FCSTD DOCUMENT  (FreeCAD 1.0R39109 (Git))
Label: MotorFinAssembly
License: Creative Commons Attribution-ShareAlike 4.0
LicenseURL: https://creativecommons.org/licenses/by-sa/4.0/
objects: App::FeaturePython×19, App::Link×18, Assembly::ViewGroup×1, Assembly::JointGroup×1, Assembly::AssemblyObject×1
EXTERNAL_REF file=CenteringRing.FCStd obj=Body
EXTERNAL_REF file=Fin.FCStd obj=Body
EXTERNAL_REF file=DowelNut.FCStd obj=Part__Feature
EXTERNAL_REF file=MMT.FCStd obj=Body
EXTERNAL_REF file=ThrustPlate-4in-AeroPack.FCStd obj=Body
EXTERNAL_REF file=Retainer-54mm-AeroPack.FCStd obj=Body

FEATURE [App::Link] Body  label="Mid Centering Ring"
  LinkedObject = -> <external CenteringRing.FCStd>#Body
FEATURE [App::FeaturePython] GroundedJoint  # Assembly grounded joint (typed FeaturePython)
  ObjectToGround = -> Body
FEATURE [App::Link] Body001  label="Fin001"
  LinkPlacement = pos=(-32.6984,-36.7997,37) rot=(0.678598,-0.281085,-0.678598;3.68962rad)
  LinkedObject = -> <external Fin.FCStd>#Body
  Placement = pos=(-32.6984,-36.7997,37) rot=(0.678598,-0.281085,-0.678598;3.68962rad)
FEATURE [App::FeaturePython] Joint  label="Fixed"  # Assembly joint (typed FeaturePython)
  Activated = true
  AngleMax = 0
  AngleMin = 0
  Detach1 = false
  Detach2 = false
  Distance = 0
  Distance2 = 0
  EnableAngleMax = false
  EnableAngleMin = false
  EnableLengthMax = false
  EnableLengthMin = false
  JointType = 0 (Fixed)
  LengthMax = 0
  LengthMin = 0
  Offset2 = pos=(0,0,0) rot=(0,0,-1;1.5708rad)
  Placement1 = pos=(-27.6426,-27.6426,5.8) rot=(0.281085,0.678598,0.678598;2.59356rad)
  Placement2 = pos=(31.2,-10.05,2.9) rot=(-0.57735,0.57735,-0.57735;4.18879rad)
  Reference1 = -> Assembly [Body.Face14,Body.Face14]
  Reference2 = -> Assembly [Body001.Face10,Body001.Face10]
FEATURE [App::Link] _0835A220_Dowel_Nuts_for_Wood  label="90835A220_Dowel Nuts for Wood"
  LinkPlacement = pos=(1.4e-15,-39.2,6.12086) rot=(0.707107,0,0.707107;3.14159rad)
  LinkedObject = -> <external DowelNut.FCStd>#Part__Feature
  Placement = pos=(1.4e-15,-39.2,6.12086) rot=(0.707107,0,0.707107;3.14159rad)
FEATURE [App::FeaturePython] Joint001  label="Fixed001"  # Assembly joint (typed FeaturePython)
  Activated = true
  AngleMax = 0
  AngleMin = 0
  Detach1 = false
  Detach2 = false
  Distance = 0
  Distance2 = 0
  EnableAngleMax = false
  EnableAngleMin = false
  EnableLengthMax = false
  EnableLengthMin = false
  JointType = 0 (Fixed)
  LengthMax = 0
  LengthMin = 0
  Placement1 = pos=(0,-39.2,0) rot=(0,0,1;0rad)
  Placement2 = pos=(-6.12086,0,0) rot=(0,-1,0;1.5708rad)
  Reference1 = -> Assembly [Body.Edge29,Body.Edge29]
  Reference2 = -> Assembly [_0835A220_Dowel_Nuts_for_Wood.Edge144,_0835A220_Dowel_Nuts_for_Wood.Edge144]
FEATURE [App::Link] Body002  label="Fin002"
  LinkPlacement = pos=(36.7997,-32.6984,37) rot=(0.678598,0.281085,-0.678598;2.59356rad)
  LinkedObject = -> <external Fin.FCStd>#Body
  Placement = pos=(36.7997,-32.6984,37) rot=(0.678598,0.281085,-0.678598;2.59356rad)
FEATURE [App::Link] Body003  label="Fin003"
  LinkPlacement = pos=(32.6984,36.7997,37) rot=(0.357407,0.862856,-0.357407;1.71777rad)
  LinkedObject = -> <external Fin.FCStd>#Body
  Placement = pos=(32.6984,36.7997,37) rot=(0.357407,0.862856,-0.357407;1.71777rad)
FEATURE [App::Link] Body004  label="Fin004"
  LinkPlacement = pos=(-36.7997,32.6984,37) rot=(-0.357407,0.862856,0.357407;1.71777rad)
  LinkedObject = -> <external Fin.FCStd>#Body
  Placement = pos=(-36.7997,32.6984,37) rot=(-0.357407,0.862856,0.357407;1.71777rad)
FEATURE [App::FeaturePython] Joint002  label="Fixed002"  # Assembly joint (typed FeaturePython)
  Activated = true
  AngleMax = 0
  AngleMin = 0
  Detach1 = false
  Detach2 = false
  Distance = 0
  Distance2 = 0
  EnableAngleMax = false
  EnableAngleMin = false
  EnableLengthMax = false
  EnableLengthMin = false
  JointType = 0 (Fixed)
  LengthMax = 0
  LengthMin = 0
  Offset2 = pos=(0,0,0) rot=(0,0,1;1.5708rad)
  Placement1 = pos=(31.2,-10.05,2.9) rot=(0,-0.707107,0.707107;3.14159rad)
  Placement2 = pos=(27.6426,-27.6426,5.8) rot=(0.357407,0.862856,0.357407;4.56541rad)
  Reference1 = -> Assembly [Body002.Face10,Body002.Face10]
  Reference2 = -> Assembly [Body.Face8,Body.Face8]
FEATURE [App::FeaturePython] Joint003  label="Fixed003"  # Assembly joint (typed FeaturePython)
  Activated = true
  AngleMax = 0
  AngleMin = 0
  Detach1 = false
  Detach2 = false
  Distance = 0
  Distance2 = 0
  EnableAngleMax = false
  EnableAngleMin = false
  EnableLengthMax = false
  EnableLengthMin = false
  JointType = 0 (Fixed)
  LengthMax = 0
  LengthMin = 0
  Offset2 = pos=(0,0,0) rot=(0,0,-1;1.5708rad)
  Placement1 = pos=(27.6426,27.6426,5.8) rot=(0.862856,-0.357407,-0.357407;1.71777rad)
  Placement2 = pos=(31.2,-10.05,2.9) rot=(0.57735,-0.57735,0.57735;2.0944rad)
  Reference1 = -> Assembly [Body.Face25,Body.Face25]
  Reference2 = -> Assembly [Body003.Face10,Body003.Face10]
FEATURE [App::FeaturePython] Joint004  label="Fixed004"  # Assembly joint (typed FeaturePython)
  Activated = true
  AngleMax = 0
  AngleMin = 0
  Detach1 = false
  Detach2 = false
  Distance = 0
  Distance2 = 0
  EnableAngleMax = false
  EnableAngleMin = false
  EnableLengthMax = false
  EnableLengthMin = false
  JointType = 0 (Fixed)
  LengthMax = 0
  LengthMin = 0
  Offset2 = pos=(0,0,0) rot=(0,0,-1;1.5708rad)
  Placement1 = pos=(-27.6426,27.6426,5.8) rot=(0.862856,0.357407,0.357407;1.71777rad)
  Placement2 = pos=(31.2,-10.05,2.9) rot=(0.57735,-0.57735,0.57735;2.0944rad)
  Reference1 = -> Assembly [Body.Face19,Body.Face19]
  Reference2 = -> Assembly [Body004.Face10,Body004.Face10]
FEATURE [App::Link] _0835A220_Dowel_Nuts_for_Wood001  label="90835A220_Dowel Nuts for Wood001"
  LinkPlacement = pos=(-1.4e-15,39.2,6.12086) rot=(0.707107,0,0.707107;3.14159rad)
  LinkedObject = -> <external DowelNut.FCStd>#Part__Feature
  Placement = pos=(-1.4e-15,39.2,6.12086) rot=(0.707107,0,0.707107;3.14159rad)
FEATURE [App::Link] _0835A220_Dowel_Nuts_for_Wood002  label="90835A220_Dowel Nuts for Wood002"
  LinkPlacement = pos=(39.2,0,6.12086) rot=(0.707107,0,0.707107;3.14159rad)
  LinkedObject = -> <external DowelNut.FCStd>#Part__Feature
  Placement = pos=(39.2,0,6.12086) rot=(0.707107,0,0.707107;3.14159rad)
FEATURE [App::Link] _0835A220_Dowel_Nuts_for_Wood003  label="90835A220_Dowel Nuts for Wood003"
  LinkPlacement = pos=(-39.2,0,6.12086) rot=(0.707107,0,0.707107;3.14159rad)
  LinkedObject = -> <external DowelNut.FCStd>#Part__Feature
  Placement = pos=(-39.2,0,6.12086) rot=(0.707107,0,0.707107;3.14159rad)
FEATURE [App::FeaturePython] Joint005  label="Fixed005"  # Assembly joint (typed FeaturePython)
  Activated = true
  AngleMax = 0
  AngleMin = 0
  Detach1 = false
  Detach2 = false
  Distance = 0
  Distance2 = 0
  EnableAngleMax = false
  EnableAngleMin = false
  EnableLengthMax = false
  EnableLengthMin = false
  JointType = 0 (Fixed)
  LengthMax = 0
  LengthMin = 0
  Placement1 = pos=(-6.12086,0,0) rot=(0,-1,0;1.5708rad)
  Placement2 = pos=(-39.2,0,0) rot=(0,0,1;0rad)
  Reference1 = -> Assembly [_0835A220_Dowel_Nuts_for_Wood003.Edge62,_0835A220_Dowel_Nuts_for_Wood003.Edge62]
  Reference2 = -> Assembly [Body.Edge30,Body.Edge30]
FEATURE [App::FeaturePython] Joint006  label="Fixed006"  # Assembly joint (typed FeaturePython)
  Activated = true
  AngleMax = 0
  AngleMin = 0
  Detach1 = false
  Detach2 = false
  Distance = 0
  Distance2 = 0
  EnableAngleMax = false
  EnableAngleMin = false
  EnableLengthMax = false
  EnableLengthMin = false
  JointType = 0 (Fixed)
  LengthMax = 0
  LengthMin = 0
  Placement1 = pos=(-6.12086,0,0) rot=(0,-1,0;1.5708rad)
  Placement2 = pos=(0,39.2,0) rot=(0,0,1;0rad)
  Reference1 = -> Assembly [_0835A220_Dowel_Nuts_for_Wood001.Edge144,_0835A220_Dowel_Nuts_for_Wood001.Edge144]
  Reference2 = -> Assembly [Body.Edge34,Body.Edge34]
FEATURE [App::FeaturePython] Joint007  label="Fixed007"  # Assembly joint (typed FeaturePython)
  Activated = true
  AngleMax = 0
  AngleMin = 0
  Detach1 = false
  Detach2 = false
  Distance = 0
  Distance2 = 0
  EnableAngleMax = false
  EnableAngleMin = false
  EnableLengthMax = false
  EnableLengthMin = false
  JointType = 0 (Fixed)
  LengthMax = 0
  LengthMin = 0
  Placement1 = pos=(-6.12086,0,0) rot=(0,-1,0;1.5708rad)
  Placement2 = pos=(39.2,0,0) rot=(0,0,1;0rad)
  Reference1 = -> Assembly [_0835A220_Dowel_Nuts_for_Wood002.Edge144,_0835A220_Dowel_Nuts_for_Wood002.Edge144]
  Reference2 = -> Assembly [Body.Edge35,Body.Edge35]
FEATURE [Assembly::ViewGroup] Exploded_Views
FEATURE [App::Link] Body005  label="Aft Centering Ring"
  LinkPlacement = pos=(1.91e-14,-7.84e-14,-267.8) rot=(0,0,1;0rad)
  LinkedObject = -> <external CenteringRing.FCStd>#Body
  Placement = pos=(1.91e-14,-7.84e-14,-267.8) rot=(0,0,1;0rad)
FEATURE [App::FeaturePython] Joint008  label="Fixed008"  # Assembly joint (typed FeaturePython)
  Activated = true
  AngleMax = 0
  AngleMin = 0
  Detach1 = false
  Detach2 = false
  Distance = 0
  Distance2 = 0
  EnableAngleMax = false
  EnableAngleMin = false
  EnableLengthMax = false
  EnableLengthMin = false
  JointType = 0 (Fixed)
  LengthMax = 0
  LengthMin = 0
  Offset2 = pos=(0,0,0) rot=(0,0,1;1.5708rad)
  Placement1 = pos=(299,-10.05,2.9) rot=(0,-0.707107,0.707107;3.14159rad)
  Placement2 = pos=(-27.6426,27.6426,5.8) rot=(0.678598,-0.281085,0.678598;2.59356rad)
  Reference1 = -> Assembly [Body004.Face6,Body004.Face6]
  Reference2 = -> Assembly [Body005.Face19,Body005.Face19]
FEATURE [App::Link] _0835A220_Dowel_Nuts_for_Wood004  label="90835A220_Dowel Nuts for Wood004"
  LinkPlacement = pos=(39.2,-7.64e-14,-261.421) rot=(0,1,0;1.5708rad)
  LinkedObject = -> <external DowelNut.FCStd>#Part__Feature
  Placement = pos=(39.2,-7.64e-14,-261.421) rot=(0,1,0;1.5708rad)
FEATURE [App::Link] _0835A220_Dowel_Nuts_for_Wood005  label="90835A220_Dowel Nuts for Wood005"
  LinkPlacement = pos=(1.85e-14,39.2,-261.421) rot=(0,1,0;1.5708rad)
  LinkedObject = -> <external DowelNut.FCStd>#Part__Feature
  Placement = pos=(1.85e-14,39.2,-261.421) rot=(0,1,0;1.5708rad)
FEATURE [App::Link] _0835A220_Dowel_Nuts_for_Wood006  label="90835A220_Dowel Nuts for Wood006"
  LinkPlacement = pos=(1.85e-14,-39.2,-261.421) rot=(0,1,0;1.5708rad)
  LinkedObject = -> <external DowelNut.FCStd>#Part__Feature
  Placement = pos=(1.85e-14,-39.2,-261.421) rot=(0,1,0;1.5708rad)
FEATURE [App::Link] _0835A220_Dowel_Nuts_for_Wood007  label="90835A220_Dowel Nuts for Wood007"
  LinkPlacement = pos=(-39.2,-7.64e-14,-261.421) rot=(0,1,0;1.5708rad)
  LinkedObject = -> <external DowelNut.FCStd>#Part__Feature
  Placement = pos=(-39.2,-7.64e-14,-261.421) rot=(0,1,0;1.5708rad)
FEATURE [App::FeaturePython] Joint009  label="Fixed009"  # Assembly joint (typed FeaturePython)
  Activated = true
  AngleMax = 0
  AngleMin = 0
  Detach1 = false
  Detach2 = false
  Distance = 0
  Distance2 = 0
  EnableAngleMax = false
  EnableAngleMin = false
  EnableLengthMax = false
  EnableLengthMin = false
  JointType = 0 (Fixed)
  LengthMax = 0
  LengthMin = 0
  Offset2 = pos=(0,0,0.9) rot=(0,0,1;0rad)
  Placement1 = pos=(-6.12086,0,0) rot=(0,-1,0;1.5708rad)
  Placement2 = pos=(0,-39.2,12.5) rot=(0,0,1;0rad)
  Reference1 = -> Assembly [_0835A220_Dowel_Nuts_for_Wood006.Edge62,_0835A220_Dowel_Nuts_for_Wood006.Edge62]
  Reference2 = -> Assembly [Body005.Edge61,Body005.Edge61]
FEATURE [App::FeaturePython] Joint010  label="Fixed010"  # Assembly joint (typed FeaturePython)
  Activated = true
  AngleMax = 0
  AngleMin = 0
  Detach1 = false
  Detach2 = false
  Distance = 0
  Distance2 = 0
  EnableAngleMax = false
  EnableAngleMin = false
  EnableLengthMax = false
  EnableLengthMin = false
  JointType = 0 (Fixed)
  LengthMax = 0
  LengthMin = 0
  Offset2 = pos=(0,0,0.9) rot=(0,0,1;0rad)
  Placement1 = pos=(-6.12086,0,0) rot=(0,-1,0;1.5708rad)
  Placement2 = pos=(0,39.2,12.5) rot=(0,0,1;0rad)
  Reference1 = -> Assembly [_0835A220_Dowel_Nuts_for_Wood005.Edge62,_0835A220_Dowel_Nuts_for_Wood005.Edge62]
  Reference2 = -> Assembly [Body005.Edge66,Body005.Edge66]
FEATURE [App::FeaturePython] Joint011  label="Fixed011"  # Assembly joint (typed FeaturePython)
  Activated = true
  AngleMax = 0
  AngleMin = 0
  Detach1 = false
  Detach2 = false
  Distance = 0
  Distance2 = 0
  EnableAngleMax = false
  EnableAngleMin = false
  EnableLengthMax = false
  EnableLengthMin = false
  JointType = 0 (Fixed)
  LengthMax = 0
  LengthMin = 0
  Offset2 = pos=(0,0,0.9) rot=(0,0,1;0rad)
  Placement1 = pos=(-6.12086,0,0) rot=(0,-1,0;1.5708rad)
  Placement2 = pos=(-39.2,0,12.5) rot=(0,0,1;0rad)
  Reference1 = -> Assembly [_0835A220_Dowel_Nuts_for_Wood007.Edge62,_0835A220_Dowel_Nuts_for_Wood007.Edge62]
  Reference2 = -> Assembly [Body005.Edge62,Body005.Edge62]
FEATURE [App::FeaturePython] Joint012  label="Fixed012"  # Assembly joint (typed FeaturePython)
  Activated = true
  AngleMax = 0
  AngleMin = 0
  Detach1 = false
  Detach2 = false
  Distance = 0
  Distance2 = 0
  EnableAngleMax = false
  EnableAngleMin = false
  EnableLengthMax = false
  EnableLengthMin = false
  JointType = 0 (Fixed)
  LengthMax = 0
  LengthMin = 0
  Offset2 = pos=(0,0,0.9) rot=(0,0,1;0rad)
  Placement1 = pos=(-6.12086,0,0) rot=(0,-1,0;1.5708rad)
  Placement2 = pos=(39.2,0,12.5) rot=(0,0,1;0rad)
  Reference1 = -> Assembly [_0835A220_Dowel_Nuts_for_Wood004.Edge62,_0835A220_Dowel_Nuts_for_Wood004.Edge62]
  Reference2 = -> Assembly [Body005.Edge67,Body005.Edge67]
FEATURE [App::Link] Body006  label="Motor Mount Tube"
  LinkPlacement = pos=(1.51e-14,-9.06e-14,-288.3) rot=(0,0,1;0rad)
  LinkedObject = -> <external MMT.FCStd>#Body
  Placement = pos=(1.51e-14,-9.06e-14,-288.3) rot=(0,0,1;0rad)
FEATURE [App::FeaturePython] Joint013  label="Fixed013"  # Assembly joint (typed FeaturePython)
  Activated = true
  AngleMax = 0
  AngleMin = 0
  Detach1 = false
  Detach2 = false
  Distance = 0
  Distance2 = 0
  EnableAngleMax = false
  EnableAngleMin = false
  EnableLengthMax = false
  EnableLengthMin = false
  JointType = 0 (Fixed)
  LengthMax = 0
  LengthMin = 0
  Offset2 = pos=(0,0,-38.1) rot=(0,0,1;0rad)
  Placement2 = pos=(0,0,-38.1) rot=(0,0,1;0rad)
  Reference1 = -> Assembly [Body006.Edge2,Body006.Edge2]
  Reference2 = -> Assembly [Body005.Edge31,Body005.Edge31]
FEATURE [App::Link] Body007  label="Thrust Plate"
  LinkPlacement = pos=(1.7e-14,-8.47e-14,-278.3) rot=(0,0,-1;0.523599rad)
  LinkedObject = -> <external ThrustPlate-4in-AeroPack.FCStd>#Body
  Placement = pos=(1.7e-14,-8.47e-14,-278.3) rot=(0,0,-1;0.523599rad)
FEATURE [App::Link] Body008  label="Retainer Body"
  LinkPlacement = pos=(1.67e-14,-8.58e-14,-280.3) rot=(0,0,1;0rad)
  LinkedObject = -> <external Retainer-54mm-AeroPack.FCStd>#Body
  Placement = pos=(1.67e-14,-8.58e-14,-280.3) rot=(0,0,1;0rad)
FEATURE [App::FeaturePython] Joint014  label="Fixed014"  # Assembly joint (typed FeaturePython)
  Activated = true
  AngleMax = 0
  AngleMin = 0
  Detach1 = false
  Detach2 = false
  Distance = 0
  Distance2 = 0
  EnableAngleMax = false
  EnableAngleMin = false
  EnableLengthMax = false
  EnableLengthMin = false
  JointType = 0 (Fixed)
  LengthMax = 0
  LengthMin = 0
  Placement1 = pos=(0,0,10.5) rot=(0,0,1;0rad)
  Reference1 = -> Assembly [Body007.Edge38,Body007.Edge38]
  Reference2 = -> Assembly [Body005.Edge23,Body005.Edge23]
FEATURE [App::FeaturePython] Joint015  label="Fixed015"  # Assembly joint (typed FeaturePython)
  Activated = true
  AngleMax = 0
  AngleMin = 0
  Detach1 = false
  Detach2 = false
  Distance = 0
  Distance2 = 0
  EnableAngleMax = false
  EnableAngleMin = false
  EnableLengthMax = false
  EnableLengthMin = false
  JointType = 0 (Fixed)
  LengthMax = 0
  LengthMin = 0
  Offset2 = pos=(0,0,0) rot=(0,0,1;0.523599rad)
  Placement2 = pos=(0,0,2) rot=(0.965926,-0.258819,0;3.14159rad)
  Reference1 = -> Assembly [Body007.Edge5,Body007.Edge5]
  Reference2 = -> Assembly [Body008.Edge94,Body008.Edge94]
FEATURE [App::FeaturePython] Joint016  label="Fixed016"  # Assembly joint (typed FeaturePython)
  Activated = true
  AngleMax = 0
  AngleMin = 0
  Detach1 = false
  Detach2 = false
  Distance = 0
  Distance2 = 0
  EnableAngleMax = false
  EnableAngleMin = false
  EnableLengthMax = false
  EnableLengthMin = false
  JointType = 0 (Fixed)
  LengthMax = 0
  LengthMin = 0
  Offset2 = pos=(0,0,-1) rot=(0,0,1;0rad)
  Placement2 = pos=(0,0,-8) rot=(1,0,0;3.14159rad)
  Reference1 = -> Assembly [Body006.Pocket.Edge2,Body006.Pocket.Edge2]
  Reference2 = -> Assembly [Body008.Pocket001.Edge104,Body008.Pocket001.Edge104]
FEATURE [App::Link] Body009  label="Body"
  LinkPlacement = pos=(1.286e-13,2.482e-13,284.3) rot=(0,0,1;0rad)
  LinkedObject = -> <external CenteringRing.FCStd>#Body
  Placement = pos=(1.286e-13,2.482e-13,284.3) rot=(0,0,1;0rad)
FEATURE [App::FeaturePython] Joint017  label="Fixed017"  # Assembly joint (typed FeaturePython)
  Activated = true
  AngleMax = 0
  AngleMin = 0
  Detach1 = false
  Detach2 = false
  Distance = 0
  Distance2 = 0
  EnableAngleMax = false
  EnableAngleMin = false
  EnableLengthMax = false
  EnableLengthMin = false
  JointType = 0 (Fixed)
  LengthMax = 0
  LengthMin = 0
  Offset2 = pos=(0,0,-25.4) rot=(0,0,1;0rad)
  Placement1 = pos=(0,0,11.6) rot=(0,0,1;0rad)
  Placement2 = pos=(0,0,584.2) rot=(0,0,1;0rad)
  Reference1 = -> Assembly [Body009.Pocket001.Edge63,Body009.Pocket001.Edge63]
  Reference2 = -> Assembly [Body006.Pocket.Edge3,Body006.Pocket.Edge3]
FEATURE [Assembly::JointGroup] Joints
  Group = -> [GroundedJoint,Joint,Joint001,Joint002,Joint003,Joint004,Joint005,Joint006,Joint007,Joint008,Joint009,Joint010,Joint011,Joint012,Joint013,Joint014,Joint015,Joint016,Joint017]
FEATURE [Assembly::AssemblyObject] Assembly
  Group = -> [Joints,Body,GroundedJoint,Body001,Joint,_0835A220_Dowel_Nuts_for_Wood,Joint001,Body002,Body003,Body004,Joint002,Joint003,Joint004,_0835A220_Dowel_Nuts_for_Wood001,_0835A220_Dowel_Nuts_for_Wood002,_0835A220_Dowel_Nuts_for_Wood003,Joint005,Joint006,Joint007,Exploded_Views,Body005,Joint008,_0835A220_Dowel_Nuts_for_Wood004,_0835A220_Dowel_Nuts_for_Wood005,_0835A220_Dowel_Nuts_for_Wood006,+14 more]
  Origin = -> Origin
  Type = Assembly

RESOLVED EXTERNAL PARTS (link-assembly join: the EXTERNAL_REF files above that resolve inside this repo's crawl, each included once):
---- part CenteringRing.FCStd = doc fcstd_97c84fd53016 ----
FCSTD DOCUMENT  (FreeCAD 1.0R39109 (Git))
Label: CenteringRing
License: Creative Commons Attribution-ShareAlike 4.0
LicenseURL: https://creativecommons.org/licenses/by-sa/4.0/
objects: Sketcher::SketchObject×3, PartDesign::Pocket×2, PartDesign::Pad×1, PartDesign::Body×1
note: 16 computed .brp shape members not serialized (recipe doc carries the construction recipe); baked Part::Feature solids carry a one-line shape summary decoded from their .brp
EXTERNAL_REF file=Variables.FCStd obj=VarSet

FEATURE [Sketcher::SketchObject] Sketch
  ArcFitTolerance = 1e-06
  AttachmentSupport = -> [XY_Plane]
  FullyConstrained = true
  MakeInternals = false
  MapMode = 5
  expr: Constraints[1] = Variables#VarSet.CR_Diameter
  sketch-geometry (1):
    g0: Circle CenterX=0 CenterY=0 CenterZ=0 NormalX=0 NormalY=0 NormalZ=1 AngleXU=0 Radius=49.25
  constraints (2):
    c: Coincident(g0,g-1)
    c: Diameter(g0) = 98.5
FEATURE [PartDesign::Pad] Pad
  Direction = (0,0,1)
  Length = 11.6
  Length2 = 10
  Profile = -> Sketch [Edge1]
  ReferenceAxis = -> Sketch [N_Axis]
  Refine = true
  Suppressed = false
  Type = 0
  expr: Length = Variables#VarSet.CR_Thickness
FEATURE [Sketcher::SketchObject] Sketch001
  ArcFitTolerance = 1e-06
  AttachmentSupport = -> [Pad]
  FullyConstrained = true
  MakeInternals = false
  MapMode = 5
  Placement = pos=(0,0,11.6) rot=(0,0,1;0rad)
  expr: Constraints[1] = Variables#VarSet.MM_OD
  sketch-geometry (1):
    g0: Circle CenterX=0 CenterY=0 CenterZ=0 NormalX=0 NormalY=0 NormalZ=1 AngleXU=0 Radius=29.15
  constraints (2):
    c: Coincident(g0,g-1)
    c: Diameter(g0) = 58.3
FEATURE [PartDesign::Pocket] Pocket
  BaseFeature = -> Pad
  Direction = (0,0,-1)
  Length = 5
  Length2 = 5
  Profile = -> Sketch001
  ReferenceAxis = -> Sketch001 [N_Axis]
  Refine = true
  Suppressed = false
  Type = 1
FEATURE [Sketcher::SketchObject] Sketch002
  ArcFitTolerance = 1e-06
  AttachmentSupport = -> [Pocket]
  ExternalGeometry = -> [Pocket]
  FullyConstrained = true
  MakeInternals = false
  MapMode = 5
  Placement = pos=(0,0,11.6) rot=(0,0,1;0rad)
  expr: Constraints[32] = Variables#VarSet.FinThickness
  expr: Constraints[3] = Variables#VarSet.BN_OD
  expr: Constraints[6] = 1
  sketch-geometry (34):
    g0: Circle CenterX=-39.2 CenterY=0 CenterZ=0 NormalX=0 NormalY=0 NormalZ=1 AngleXU=0 Radius=4.95
    g1: Circle [constr] CenterX=0 CenterY=0 CenterZ=0 NormalX=0 NormalY=0 NormalZ=1 AngleXU=0 Radius=39.2
    g2: Circle CenterX=-49.25 CenterY=0 CenterZ=0 NormalX=0 NormalY=0 NormalZ=1 AngleXU=0 Radius=0.5
    g3: Circle CenterX=-29.15 CenterY=0 CenterZ=0 NormalX=0 NormalY=0 NormalZ=1 AngleXU=0 Radius=0.5
    g4: Circle CenterX=0 CenterY=49.25 CenterZ=0 NormalX=0 NormalY=0 NormalZ=1 AngleXU=0 Radius=0.5
    g5: Circle CenterX=49.25 CenterY=0 CenterZ=0 NormalX=0 NormalY=0 NormalZ=1 AngleXU=0 Radius=0.5
    g6: Circle CenterX=0 CenterY=-49.25 CenterZ=0 NormalX=0 NormalY=0 NormalZ=1 AngleXU=0 Radius=0.5
    g7: Circle CenterX=0 CenterY=39.2 CenterZ=0 NormalX=0 NormalY=0 NormalZ=1 AngleXU=0 Radius=4.95
    g8: Circle CenterX=39.2 CenterY=0 CenterZ=0 NormalX=0 NormalY=0 NormalZ=1 AngleXU=0 Radius=4.95
    g9: Circle CenterX=0 CenterY=-39.2 CenterZ=0 NormalX=0 NormalY=0 NormalZ=1 AngleXU=0 Radius=4.95
    g10: LineSegment StartX=-32.714 StartY=36.8152 StartZ=0 EndX=-36.8152 EndY=32.714 EndZ=0
    g11: LineSegment StartX=-36.8152 StartY=32.714 StartZ=0 EndX=-29.6932 EndY=25.592 EndZ=0
    g12: LineSegment StartX=-29.6932 StartY=25.592 StartZ=0 EndX=-25.592 EndY=29.6932 EndZ=0
    g13: LineSegment StartX=-25.592 StartY=29.6932 StartZ=0 EndX=-32.714 EndY=36.8152 EndZ=0
    g14: LineSegment [constr] StartX=-32.714 StartY=36.8152 StartZ=0 EndX=0 EndY=49.25 EndZ=0
    g15: LineSegment [constr] StartX=-36.8152 StartY=32.714 StartZ=0 EndX=-49.25 EndY=0 EndZ=0
    g16: LineSegment StartX=36.8152 StartY=32.714 StartZ=0 EndX=32.714 EndY=36.8152 EndZ=0
    g17: LineSegment StartX=32.714 StartY=36.8152 StartZ=0 EndX=25.592 EndY=29.6932 EndZ=0
    g18: LineSegment StartX=25.592 StartY=29.6932 StartZ=0 EndX=29.6932 EndY=25.592 EndZ=0
    g19: LineSegment StartX=29.6932 StartY=25.592 StartZ=0 EndX=36.8152 EndY=32.714 EndZ=0
    g20: LineSegment [constr] StartX=32.714 StartY=36.8152 StartZ=0 EndX=0 EndY=49.25 EndZ=0
    g21: LineSegment [constr] StartX=36.8152 StartY=32.714 StartZ=0 EndX=49.25 EndY=0 EndZ=0
    g22: LineSegment StartX=32.714 StartY=-36.8152 StartZ=0 EndX=36.8152 EndY=-32.714 EndZ=0
    g23: LineSegment StartX=36.8152 StartY=-32.714 StartZ=0 EndX=29.6932 EndY=-25.592 EndZ=0
    g24: LineSegment StartX=29.6932 StartY=-25.592 StartZ=0 EndX=25.592 EndY=-29.6932 EndZ=0
    g25: LineSegment StartX=25.592 StartY=-29.6932 StartZ=0 EndX=32.714 EndY=-36.8152 EndZ=0
    g26: LineSegment [constr] StartX=36.8152 StartY=-32.714 StartZ=0 EndX=49.25 EndY=0 EndZ=0
    g27: LineSegment [constr] StartX=32.714 StartY=-36.8152 StartZ=0 EndX=0 EndY=-49.25 EndZ=0
    g28: LineSegment StartX=-36.8152 StartY=-32.714 StartZ=0 EndX=-32.714 EndY=-36.8152 EndZ=0
    g29: LineSegment StartX=-32.714 StartY=-36.8152 StartZ=0 EndX=-25.592 EndY=-29.6932 EndZ=0
    g30: LineSegment StartX=-25.592 StartY=-29.6932 StartZ=0 EndX=-29.6932 EndY=-25.592 EndZ=0
    g31: LineSegment StartX=-29.6932 StartY=-25.592 StartZ=0 EndX=-36.8152 EndY=-32.714 EndZ=0
    g32: LineSegment [constr] StartX=-32.714 StartY=-36.8152 StartZ=0 EndX=0 EndY=-49.25 EndZ=0
    g33: LineSegment [constr] StartX=-36.8152 StartY=-32.714 StartZ=0 EndX=-49.25 EndY=0 EndZ=0
  constraints (92):
    c: Coincident(g1,g-1)
    c: PointOnObject(g0,g1)
    c: PointOnObject(g0,g-1)
    c: Diameter(g0) = 9.9
    c: PointOnObject(g2,g-3)
    c: PointOnObject(g3,g-4)
    c: Diameter(g2) = 1
    c: PointOnObject(g2,g-1)
    c: Diameter(g3) = 1
    c: Equal(g2,g4)
    c: Equal(g2,g5)
    c: Equal(g2,g6)
    c: PointOnObject(g5,g-1)
    c: PointOnObject(g5,g-3)
    c: PointOnObject(g4,g-2)
    c: PointOnObject(g4,g-3)
    c: PointOnObject(g6,g-2)
    c: PointOnObject(g6,g-3)
    c: Symmetric(g3,g2,g0)
    c: Equal(g0,g7)
    c: Equal(g0,g8)
    c: Equal(g0,g9)
    c: PointOnObject(g7,g-2)
    c: PointOnObject(g7,g1)
    c: PointOnObject(g8,g-1)
    c: PointOnObject(g8,g1)
    c: PointOnObject(g9,g-2)
    c: PointOnObject(g9,g1)
    c: Coincident(g10,g11)
    c: Coincident(g11,g12)
    c: Coincident(g12,g13)
    c: Coincident(g13,g10)
    c: Distance(g10,g10) = 5.8
    c: Equal(g12,g10)
    c: Perpendicular(g13,g10)
    c: Perpendicular(g11,g12)
    c: PointOnObject(g11,g1)
    c: PointOnObject(g12,g1)
    c: PointOnObject(g10,g-3)
    c: Coincident(g14,g10)
    c: Coincident(g14,g4)
    c: Coincident(g15,g10)
    c: Coincident(g15,g2)
    c: Equal(g15,g14)
    c: Coincident(g16,g17)
    c: Coincident(g22,g23)
    c: Coincident(g28,g29)
    c: Coincident(g17,g18)
    c: Coincident(g23,g24)
    c: Coincident(g29,g30)
    c: Coincident(g18,g19)
    c: Coincident(g24,g25)
    c: Coincident(g30,g31)
    c: Coincident(g19,g16)
    c: Coincident(g25,g22)
    c: Coincident(g31,g28)
    c: Distance(g16,g16) = 5.8
    c: Distance(g22,g22) = 5.8
    c: Distance(g28,g28) = 5.8
    c: Equal(g18,g16)
    c: Equal(g24,g22)
    c: Equal(g30,g28)
    c: Perpendicular(g19,g16)
    c: Perpendicular(g25,g22)
    c: Perpendicular(g31,g28)
    c: Perpendicular(g17,g18)
    c: Perpendicular(g23,g24)
    c: Perpendicular(g29,g30)
    c: Coincident(g21,g16)
    c: Coincident(g27,g22)
    c: Coincident(g33,g28)
    c: Coincident(g20,g16)
    c: Coincident(g26,g22)
    c: Coincident(g32,g28)
    c: Equal(g20,g21)
    c: Equal(g26,g27)
    c: Equal(g32,g33)
    c: PointOnObject(g16,g-3)
    c: PointOnObject(g18,g1)
    c: PointOnObject(g17,g1)
    c: Coincident(g20,g4)
    c: Coincident(g21,g5)
    c: Coincident(g33,g2)
    c: Coincident(g32,g6)
    c: Coincident(g27,g6)
    c: Coincident(g26,g5)
    c: PointOnObject(g23,g1)
    c: PointOnObject(g24,g1)
    c: PointOnObject(g22,g-3)
    c: PointOnObject(g30,g1)
    c: PointOnObject(g29,g1)
    c: PointOnObject(g28,g-3)
FEATURE [PartDesign::Pocket] Pocket001
  BaseFeature = -> Pocket
  Direction = (0,0,-1)
  Length = 5
  Length2 = 5
  Profile = -> Sketch002
  ReferenceAxis = -> Sketch002 [N_Axis]
  Refine = true
  Suppressed = false
  Type = 1
FEATURE [PartDesign::Body] Body
  AllowCompound = false
  Group = -> [Sketch,Pad,Sketch001,Pocket,Sketch002,Pocket001]
  Origin = -> Origin
  Tip = -> Pocket001
---- part Fin.FCStd = doc fcstd_0649d5bec78a ----
FCSTD DOCUMENT  (FreeCAD 1.0R39109 (Git))
Label: Fin
License: Creative Commons Attribution-ShareAlike 4.0
LicenseURL: https://creativecommons.org/licenses/by-sa/4.0/
objects: Sketcher::SketchObject×1, PartDesign::Pad×1, PartDesign::Body×1
note: 6 computed .brp shape members not serialized (recipe doc carries the construction recipe); baked Part::Feature solids carry a one-line shape summary decoded from their .brp
EXTERNAL_REF file=Variables.FCStd obj=VarSet

FEATURE [Sketcher::SketchObject] Sketch
  ArcFitTolerance = 1e-06
  AttachmentSupport = -> [XY_Plane]
  FullyConstrained = true
  MakeInternals = false
  MapMode = 5
  expr: Constraints[23] = Variables#VarSet.Fin_TabHeight
  expr: Constraints[24] = Variables#VarSet.Fin_TabHeight / 2
  expr: Constraints[26] = Variables#VarSet.CR_Thickness
  expr: Constraints[27] = Variables#VarSet.Fin_MiddleCR
  expr: Constraints[28] = Variables#VarSet.Fin_TabHeight / 2
  expr: Constraints[29] = Variables#VarSet.Fin_RootChord
  expr: Constraints[30] = Variables#VarSet.Fin_TipChord
  expr: Constraints[31] = Variables#VarSet.Fin_TabHeight / 2
  expr: Constraints[32] = Variables#VarSet.CR_Thickness
  expr: Constraints[33] = Variables#VarSet.Fin_Height
  expr: Constraints[34] = Variables#VarSet.Fin_Sweep
  sketch-geometry (12):
    g0: LineSegment StartX=0 StartY=-20.1 StartZ=0 EndX=0 EndY=0 EndZ=0
    g1: LineSegment StartX=0 StartY=0 StartZ=0 EndX=114.3 EndY=127 EndZ=0
    g2: LineSegment StartX=114.3 StartY=127 StartZ=0 EndX=266.7 EndY=127 EndZ=0
    g3: LineSegment StartX=266.7 StartY=127 StartZ=0 EndX=304.8 EndY=0 EndZ=0
    g4: LineSegment StartX=304.8 StartY=0 StartZ=0 EndX=304.8 EndY=-10.05 EndZ=0
    g5: LineSegment StartX=304.8 StartY=-10.05 StartZ=0 EndX=293.2 EndY=-10.05 EndZ=0
    g6: LineSegment StartX=293.2 StartY=-10.05 StartZ=0 EndX=293.2 EndY=-20.1 EndZ=0
    g7: LineSegment StartX=293.2 StartY=-20.1 StartZ=0 EndX=37 EndY=-20.1 EndZ=0
    g8: LineSegment StartX=37 StartY=-20.1 StartZ=0 EndX=37 EndY=-10.05 EndZ=0
    g9: LineSegment StartX=37 StartY=-10.05 StartZ=0 EndX=25.4 EndY=-10.05 EndZ=0
    g10: LineSegment StartX=25.4 StartY=-10.05 StartZ=0 EndX=25.4 EndY=-20.1 EndZ=0
    g11: LineSegment StartX=25.4 StartY=-20.1 StartZ=0 EndX=0 EndY=-20.1 EndZ=0
  constraints (35):
    c: PointOnObject(g0,g-2)
    c: Coincident(g0,g-1)
    c: Coincident(g0,g1)
    c: Coincident(g1,g2)
    c: Horizontal(g2)
    c: Coincident(g2,g3)
    c: PointOnObject(g3,g-1)
    c: Coincident(g3,g4)
    c: Vertical(g4)
    c: Coincident(g4,g5)
    c: Horizontal(g5)
    c: Coincident(g5,g6)
    c: Vertical(g6)
    c: Coincident(g6,g7)
    c: Horizontal(g7)
    c: Coincident(g7,g8)
    c: Vertical(g8)
    c: Coincident(g8,g9)
    c: Horizontal(g9)
    c: Coincident(g9,g10)
    c: Vertical(g10)
    c: Coincident(g10,g11)
    c: Coincident(g11,g0)
    c: DistanceY(g0,g0) = 20.1
    c: DistanceY(g10,g9) = 10.05
    c: Horizontal(g11)
    c: DistanceX(g9,g8) = 11.6
    c: DistanceX(g0,g10) = 25.4
    c: DistanceY(g7,g8) = 10.05
    c: DistanceX(g0,g3) = 304.8
    c: DistanceX(g1,g2) = 152.4
    c: DistanceY(g6,g5) = 10.05
    c: DistanceX(g5,g4) = 11.6
    c: DistanceY(g0,g1) = 127
    c: DistanceX(g0,g1) = 114.3
FEATURE [PartDesign::Pad] Pad
  Direction = (0,0,1)
  Length = 5.8
  Length2 = 10
  Profile = -> Sketch
  ReferenceAxis = -> Sketch [N_Axis]
  Refine = true
  Suppressed = false
  Type = 0
  expr: Length = Variables#VarSet.FinThickness
FEATURE [PartDesign::Body] Body
  AllowCompound = false
  Group = -> [Sketch,Pad]
  Origin = -> Origin
  Tip = -> Pad
---- part MMT.FCStd = doc fcstd_de43e85ebf3a ----
FCSTD DOCUMENT  (FreeCAD 1.0R39319 (Git))
Label: MMT
License: Creative Commons Attribution-ShareAlike 4.0
LicenseURL: https://creativecommons.org/licenses/by-sa/4.0/
objects: Sketcher::SketchObject×2, PartDesign::Pad×1, PartDesign::Pocket×1, PartDesign::Body×1
note: 11 computed .brp shape members not serialized (recipe doc carries the construction recipe); baked Part::Feature solids carry a one-line shape summary decoded from their .brp

FEATURE [Sketcher::SketchObject] Sketch
  ArcFitTolerance = 1e-06
  AttachmentSupport = -> [XY_Plane]
  FullyConstrained = true
  MakeInternals = false
  MapMode = 5
  expr: Constraints[1] = 54 mm + 0.062 in * 2
  sketch-geometry (1):
    g0: Circle CenterX=0 CenterY=0 CenterZ=0 NormalX=0 NormalY=0 NormalZ=1 AngleXU=0 Radius=28.5748
  constraints (2):
    c: Coincident(g0,g-1)
    c: Diameter(g0) = 57.1496
FEATURE [PartDesign::Pad] Pad
  Direction = (0,0,1)
  Length = 609.6
  Length2 = 10
  Profile = -> Sketch
  ReferenceAxis = -> Sketch [N_Axis]
  Refine = true
  Suppressed = false
  Type = 0
FEATURE [Sketcher::SketchObject] Sketch001
  ArcFitTolerance = 1e-06
  AttachmentSupport = -> [Pad]
  FullyConstrained = true
  MakeInternals = false
  MapMode = 5
  Placement = pos=(0,0,609.6) rot=(0,0,1;0rad)
  sketch-geometry (1):
    g0: Circle CenterX=0 CenterY=0 CenterZ=0 NormalX=0 NormalY=0 NormalZ=1 AngleXU=0 Radius=27
  constraints (2):
    c: Coincident(g0,g-1)
    c: Diameter(g0) = 54
FEATURE [PartDesign::Pocket] Pocket
  BaseFeature = -> Pad
  Direction = (0,0,-1)
  Length = 5
  Length2 = 5
  Profile = -> Sketch001
  ReferenceAxis = -> Sketch001 [N_Axis]
  Refine = true
  Suppressed = false
  Type = 1
FEATURE [PartDesign::Body] Body
  AllowCompound = false
  Group = -> [Sketch,Pad,Sketch001,Pocket]
  Origin = -> Origin
  Tip = -> Pocket
---- part Retainer-54mm-AeroPack.FCStd = doc fcstd_b404d5fea255 ----
FCSTD DOCUMENT  (FreeCAD 1.0R39109 (Git))
Label: Retainer-54mm-AeroPack
License: Creative Commons Attribution-ShareAlike 4.0
LicenseURL: https://creativecommons.org/licenses/by-sa/4.0/
objects: Sketcher::SketchObject×3, PartDesign::Pocket×2, Part::FeaturePython×1, PartDesign::FeatureBase×1, PartDesign::Pad×1, PartDesign::Body×1
note: 19 computed .brp shape members not serialized (recipe doc carries the construction recipe); baked Part::Feature solids carry a one-line shape summary decoded from their .brp

FEATURE [Sketcher::SketchObject] Sketch
  ArcFitTolerance = 1e-06
  AttachmentSupport = -> [XY_Plane]
  FullyConstrained = true
  MakeInternals = false
  MapMode = 5
  sketch-geometry (14):
    g0: Circle CenterX=0 CenterY=0 CenterZ=0 NormalX=0 NormalY=0 NormalZ=1 AngleXU=0 Radius=37.8
    g1: Circle [constr] CenterX=0 CenterY=0 CenterZ=0 NormalX=0 NormalY=0 NormalZ=1 AngleXU=0 Radius=33.75
    g2: Circle CenterX=-33.75 CenterY=0 CenterZ=0 NormalX=0 NormalY=0 NormalZ=1 AngleXU=0 Radius=1
    g3: Circle CenterX=-16.875 CenterY=29.2284 CenterZ=0 NormalX=0 NormalY=0 NormalZ=1 AngleXU=0 Radius=1
    g4: Circle CenterX=16.875 CenterY=29.2284 CenterZ=0 NormalX=0 NormalY=0 NormalZ=1 AngleXU=0 Radius=1
    g5: Circle CenterX=33.75 CenterY=-3.6e-15 CenterZ=0 NormalX=0 NormalY=0 NormalZ=1 AngleXU=0 Radius=1
    g6: Circle CenterX=16.875 CenterY=-29.2284 CenterZ=0 NormalX=0 NormalY=0 NormalZ=1 AngleXU=0 Radius=1
    g7: Circle CenterX=-16.875 CenterY=-29.2284 CenterZ=0 NormalX=0 NormalY=0 NormalZ=1 AngleXU=0 Radius=1
    g8: LineSegment [constr] StartX=-33.75 StartY=0 StartZ=0 EndX=-16.875 EndY=29.2284 EndZ=0
    g9: LineSegment [constr] StartX=-16.875 StartY=29.2284 StartZ=0 EndX=16.875 EndY=29.2284 EndZ=0
    g10: LineSegment [constr] StartX=16.875 StartY=29.2284 StartZ=0 EndX=33.75 EndY=-3.6e-15 EndZ=0
    g11: LineSegment [constr] StartX=33.75 StartY=-3.6e-15 StartZ=0 EndX=16.875 EndY=-29.2284 EndZ=0
    g12: LineSegment [constr] StartX=16.875 StartY=-29.2284 StartZ=0 EndX=-16.875 EndY=-29.2284 EndZ=0
    g13: LineSegment [constr] StartX=-16.875 StartY=-29.2284 StartZ=0 EndX=-33.75 EndY=0 EndZ=0
  constraints (34):
    c: Coincident(g0,g-1)
    c: Diameter(g0) = 75.6
    c: Coincident(g1,g0)
    c: Diameter(g1) = 67.5
    c: PointOnObject(g2,g1)
    c: Diameter(g2) = 2
    c: PointOnObject(g2,g-1)
    c: Diameter(g3) = 2
    c: Diameter(g4) = 2
    c: Diameter(g5) = 2
    c: Diameter(g6) = 2
    c: Diameter(g7) = 2
    c: PointOnObject(g3,g1)
    c: PointOnObject(g4,g1)
    c: PointOnObject(g5,g1)
    c: PointOnObject(g6,g1)
    c: PointOnObject(g7,g1)
    c: Coincident(g8,g2)
    c: Coincident(g8,g3)
    c: Coincident(g9,g3)
    c: Coincident(g9,g4)
    c: Coincident(g10,g4)
    c: Coincident(g10,g5)
    c: Coincident(g11,g5)
    c: Coincident(g11,g6)
    c: Coincident(g12,g6)
    c: Coincident(g12,g7)
    c: Coincident(g13,g7)
    c: Coincident(g13,g2)
    c: Equal(g8,g9)
    c: Equal(g9,g10)
    c: Equal(g10,g11)
    c: Equal(g11,g12)
    c: Equal(g12,g13)
FEATURE [Part::FeaturePython] ThreadedRod  label="63x18.5-ThreadedRod"  # WARN: FeaturePython — macro-defined, semantics opaque (R4)
  BaseObject = -> XY_Plane
  Diameter = 29
  DiameterCustom = 63
  Invert = true
  LeftHanded = false
  Length = 18.5
  MatchOuter = false
  OffsetAngle = 0
  PitchCustom = 2
  Thread = true
  Type = 4
FEATURE [PartDesign::FeatureBase] BaseFeature
  BaseFeature = -> ThreadedRod
  Suppressed = false
FEATURE [PartDesign::Pad] Pad
  BaseFeature = -> BaseFeature
  Direction = (0,0,1)
  Length = 2
  Length2 = 10
  Profile = -> Sketch
  ReferenceAxis = -> Sketch [N_Axis]
  Refine = true
  Suppressed = false
  Type = 0
FEATURE [Sketcher::SketchObject] Sketch001
  ArcFitTolerance = 1e-06
  AttachmentSupport = -> [BaseFeature]
  FullyConstrained = true
  MakeInternals = false
  MapMode = 5
  Placement = pos=(0,0,-18.5) rot=(1,0,0;3.14159rad)
  sketch-geometry (1):
    g0: Circle CenterX=0 CenterY=0 CenterZ=0 NormalX=0 NormalY=0 NormalZ=1 AngleXU=0 Radius=27.125
  constraints (2):
    c: Coincident(g0,g-1)
    c: Diameter(g0) = 54.25
FEATURE [PartDesign::Pocket] Pocket
  BaseFeature = -> Pad
  Direction = (0,0,1)
  Length = 5
  Length2 = 5
  Profile = -> Sketch001
  ReferenceAxis = -> Sketch001 [N_Axis]
  Refine = true
  Suppressed = false
  Type = 1
FEATURE [Sketcher::SketchObject] Sketch002
  ArcFitTolerance = 1e-06
  AttachmentSupport = -> [Pocket]
  FullyConstrained = true
  MakeInternals = false
  MapMode = 5
  Placement = pos=(0,0,-18.5) rot=(1,0,0;3.14159rad)
  sketch-geometry (1):
    g0: Circle CenterX=0 CenterY=0 CenterZ=0 NormalX=0 NormalY=0 NormalZ=1 AngleXU=0 Radius=29.6
  constraints (2):
    c: Coincident(g0,g-1)
    c: Diameter(g0) = 59.2
FEATURE [PartDesign::Pocket] Pocket001
  BaseFeature = -> Pocket
  Direction = (0,0,1)
  Length = 9.5
  Length2 = 5
  Profile = -> Sketch002
  ReferenceAxis = -> Sketch002 [N_Axis]
  Refine = true
  Suppressed = false
  Type = 0
FEATURE [PartDesign::Body] Body
  AllowCompound = false
  BaseFeature = -> ThreadedRod
  Group = -> [BaseFeature,Sketch,Pad,Sketch001,Pocket,Sketch002,Pocket001]
  Origin = -> Origin
  Tip = -> Pocket001
---- part ThrustPlate-4in-AeroPack.FCStd = doc fcstd_23e2ba1e50ca ----
FCSTD DOCUMENT  (FreeCAD 1.0R39109 (Git))
Label: ThrustPlate-4in-AeroPack
License: Creative Commons Attribution-ShareAlike 4.0
LicenseURL: https://creativecommons.org/licenses/by-sa/4.0/
objects: Sketcher::SketchObject×3, PartDesign::Pad×2, PartDesign::Chamfer×2, PartDesign::Pocket×1, PartDesign::Body×1
note: 22 computed .brp shape members not serialized (recipe doc carries the construction recipe); baked Part::Feature solids carry a one-line shape summary decoded from their .brp

FEATURE [Sketcher::SketchObject] Sketch
  ArcFitTolerance = 1e-06
  AttachmentSupport = -> [XY_Plane]
  FullyConstrained = true
  MakeInternals = false
  MapMode = 5
  sketch-geometry (1):
    g0: Circle CenterX=0 CenterY=0 CenterZ=0 NormalX=0 NormalY=0 NormalZ=1 AngleXU=0 Radius=50.425
  constraints (2):
    c: Coincident(g0,g-1)
    c: Diameter(g0) = 100.85
FEATURE [PartDesign::Pad] Pad
  Direction = (0,0,1)
  Length = 7
  Length2 = 10
  Profile = -> Sketch
  ReferenceAxis = -> Sketch [N_Axis]
  Refine = true
  Suppressed = false
  Type = 0
FEATURE [Sketcher::SketchObject] Sketch001
  ArcFitTolerance = 1e-06
  AttachmentSupport = -> [Pad]
  FullyConstrained = true
  MakeInternals = false
  MapMode = 5
  Placement = pos=(0,0,7) rot=(0,0,1;0rad)
  sketch-geometry (1):
    g0: Circle CenterX=0 CenterY=0 CenterZ=0 NormalX=0 NormalY=0 NormalZ=1 AngleXU=0 Radius=49.3
  constraints (2):
    c: Coincident(g0,g-1)
    c: Diameter(g0) = 98.6
FEATURE [PartDesign::Pad] Pad001
  BaseFeature = -> Pad
  Direction = (0,0,1)
  Length = 3.5
  Length2 = 10
  Profile = -> Sketch001
  ReferenceAxis = -> Sketch001 [N_Axis]
  Refine = true
  Suppressed = false
  Type = 0
FEATURE [PartDesign::Chamfer] Chamfer
  Angle = 45
  Base = -> Pad001 [Edge2]
  BaseFeature = -> Pad001
  ChamferType = 0
  FlipDirection = false
  Refine = true
  Size = 3.5
  Size2 = 1
  SupportTransform = false
  Suppressed = false
  UseAllEdges = false
FEATURE [Sketcher::SketchObject] Sketch002
  ArcFitTolerance = 1e-06
  AttachmentSupport = -> [Chamfer]
  FullyConstrained = true
  MakeInternals = false
  MapMode = 5
  Placement = pos=(0,0,10.5) rot=(0,0,1;0rad)
  sketch-geometry (23):
    g0: Circle CenterX=0 CenterY=0 CenterZ=0 NormalX=0 NormalY=0 NormalZ=1 AngleXU=0 Radius=27.8
    g1: Circle CenterX=-43.3 CenterY=0 CenterZ=0 NormalX=0 NormalY=0 NormalZ=1 AngleXU=0 Radius=2.5
    g2: Circle [constr] CenterX=0 CenterY=0 CenterZ=0 NormalX=0 NormalY=0 NormalZ=1 AngleXU=0 Radius=43.3
    g3: Circle CenterX=21.65 CenterY=37.4989 CenterZ=0 NormalX=0 NormalY=0 NormalZ=1 AngleXU=0 Radius=2.5
    g4: Circle CenterX=21.65 CenterY=-37.4989 CenterZ=0 NormalX=0 NormalY=0 NormalZ=1 AngleXU=0 Radius=2.5
    g5: LineSegment [constr] StartX=-43.3 StartY=0 StartZ=0 EndX=21.65 EndY=37.4989 EndZ=0
    g6: LineSegment [constr] StartX=21.65 StartY=-37.4989 StartZ=0 EndX=21.65 EndY=37.4989 EndZ=0
    g7: LineSegment [constr] StartX=-43.3 StartY=0 StartZ=0 EndX=21.65 EndY=-37.4989 EndZ=0
    g8: Circle [constr] CenterX=0 CenterY=0 CenterZ=0 NormalX=0 NormalY=0 NormalZ=1 AngleXU=0 Radius=34.3
    g9: Circle CenterX=-29.7047 CenterY=17.15 CenterZ=0 NormalX=0 NormalY=0 NormalZ=1 AngleXU=0 Radius=1.75
    g10: Circle CenterX=1.1e-15 CenterY=34.3 CenterZ=0 NormalX=0 NormalY=0 NormalZ=1 AngleXU=0 Radius=1.75
    g11: Circle CenterX=29.7047 CenterY=17.15 CenterZ=0 NormalX=0 NormalY=0 NormalZ=1 AngleXU=0 Radius=1.75
    g12: Circle CenterX=29.7047 CenterY=-17.15 CenterZ=0 NormalX=0 NormalY=0 NormalZ=1 AngleXU=0 Radius=1.75
    g13: Circle CenterX=-3.6e-15 CenterY=-34.3 CenterZ=0 NormalX=0 NormalY=0 NormalZ=1 AngleXU=0 Radius=1.75
    g14: Circle CenterX=-29.7047 CenterY=-17.15 CenterZ=0 NormalX=0 NormalY=0 NormalZ=1 AngleXU=0 Radius=1.75
    g15: LineSegment [constr] StartX=-29.7047 StartY=17.15 StartZ=0 EndX=0 EndY=34.3 EndZ=0
    g16: LineSegment [constr] StartX=1.1e-15 StartY=34.3 StartZ=0 EndX=29.7047 EndY=17.15 EndZ=0
    g17: LineSegment [constr] StartX=29.7047 StartY=17.15 StartZ=0 EndX=29.7047 EndY=-17.15 EndZ=0
    g18: LineSegment [constr] StartX=-3.6e-15 StartY=-34.3 StartZ=0 EndX=29.7047 EndY=-17.15 EndZ=0
    g19: LineSegment [constr] StartX=-29.7047 StartY=-17.15 StartZ=0 EndX=-3.6e-15 EndY=-34.3 EndZ=0
    g20: LineSegment [constr] StartX=-29.7047 StartY=17.15 StartZ=0 EndX=-29.7047 EndY=-17.15 EndZ=0
    g21: LineSegment [constr] StartX=-43.3 StartY=0 StartZ=0 EndX=-29.7047 EndY=-17.15 EndZ=0
    g22: LineSegment [constr] StartX=-43.3 StartY=0 StartZ=0 EndX=-29.7047 EndY=17.15 EndZ=0
  constraints (55):
    c: Coincident(g0,g-1)
    c: Diameter(g0) = 55.6
    c: PointOnObject(g1,g-1)
    c: Diameter(g1) = 5
    c: Coincident(g2,g0)
    c: Diameter(g2) = 86.6
    c: PointOnObject(g1,g2)
    c: Diameter(g3) = 5
    c: Diameter(g4) = 5
    c: PointOnObject(g3,g2)
    c: PointOnObject(g4,g2)
    c: Coincident(g5,g1)
    c: Coincident(g5,g3)
    c: Coincident(g6,g4)
    c: Coincident(g6,g3)
    c: Coincident(g7,g1)
    c: Coincident(g7,g4)
    c: Equal(g7,g5)
    c: Equal(g5,g6)
    c: Coincident(g8,g0)
    c: Diameter(g8) = 68.6
    c: PointOnObject(g9,g8)
    c: Diameter(g9) = 3.5
    c: Diameter(g10) = 3.5
    c: Diameter(g11) = 3.5
    c: Diameter(g12) = 3.5
    c: Diameter(g13) = 3.5
    c: Diameter(g14) = 3.5
    c: Coincident(g15,g9)
    c: Coincident(g15,g10)
    c: Coincident(g16,g10)
    c: Coincident(g16,g11)
    c: Coincident(g17,g11)
    c: Coincident(g17,g12)
    c: Coincident(g18,g13)
    c: Coincident(g18,g12)
    c: Coincident(g19,g14)
    c: Coincident(g19,g13)
    c: Coincident(g20,g9)
    c: Coincident(g20,g14)
    c: PointOnObject(g10,g8)
    c: PointOnObject(g11,g8)
    c: PointOnObject(g12,g8)
    c: PointOnObject(g13,g8)
    c: PointOnObject(g14,g8)
    c: Equal(g15,g16)
    c: Equal(g16,g17)
    c: Equal(g17,g18)
    c: Equal(g18,g19)
    c: Equal(g19,g20)
    c: Coincident(g21,g1)
    c: Coincident(g21,g14)
    c: Coincident(g22,g1)
    c: Coincident(g22,g9)
    c: Equal(g22,g21)
FEATURE [PartDesign::Pocket] Pocket
  BaseFeature = -> Chamfer
  Direction = (0,0,-1)
  Length = 5
  Length2 = 5
  Profile = -> Sketch002
  ReferenceAxis = -> Sketch002 [N_Axis]
  Refine = true
  Suppressed = false
  Type = 1
FEATURE [PartDesign::Chamfer] Chamfer001
  Angle = 70
  Base = -> Pocket [Edge10,Edge8,Edge16]
  BaseFeature = -> Pocket
  ChamferType = 2
  FlipDirection = false
  Refine = true
  Size = 1
  Size2 = 1
  SupportTransform = false
  Suppressed = false
  UseAllEdges = false
FEATURE [PartDesign::Body] Body
  AllowCompound = false
  Group = -> [Sketch,Pad,Sketch001,Pad001,Chamfer,Sketch002,Pocket,Chamfer001]
  Origin = -> Origin
  Tip = -> Chamfer001
